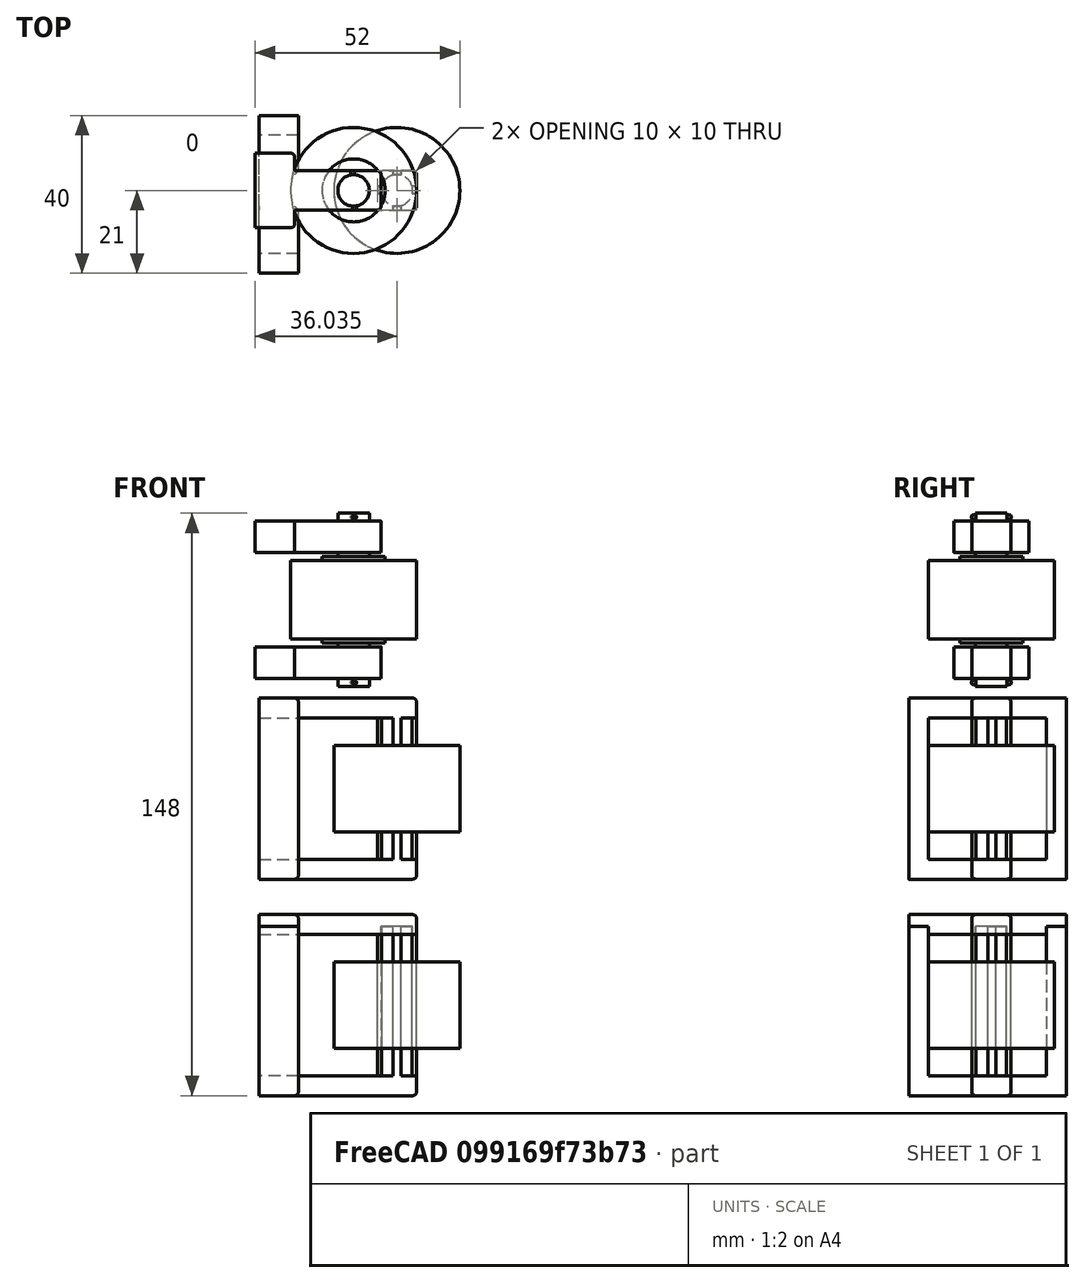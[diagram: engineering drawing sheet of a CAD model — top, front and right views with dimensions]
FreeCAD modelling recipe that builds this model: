
FCSTD DOCUMENT  (FreeCAD 0.17R13541 (Git))
Label: Electrical Tape Holder
License: All rights reserved
LicenseURL: http://en.wikipedia.org/wiki/All_rights_reserved
objects: Part::Box×98, Part::Cut×44, Part::MultiFuse×40, Part::Cylinder×35, Part::Fillet×17
note: 234 computed .brp shape members not serialized (recipe doc carries the construction recipe); baked Part::Feature solids carry a one-line shape summary decoded from their .brp

FEATURE [Part::Cylinder] Cylinder  label="Tape Holder"
  Angle = 360
  AttacherType = Attacher::AttachEngine3D
  Height = 22
  Placement = pos=(0,0,-1) rot=(0,0,1;0rad)
  Radius = 16
FEATURE [Part::Cylinder] Cylinder002  label="Tape Rotation Bar"
  Angle = 360
  AttacherType = Attacher::AttachEngine3D
  Height = 22
  Placement = pos=(0,0,-1) rot=(0,0,1;0rad)
  Radius = 8
FEATURE [Part::Cylinder] Cylinder003  label="Tape Rotation Bar Support"
  Angle = 360
  AttacherType = Attacher::AttachEngine3D
  Height = 44
  Placement = pos=(0,0,-12) rot=(0,0,1;0rad)
  Radius = 4
FEATURE [Part::Cylinder] Cylinder004  label="Tape Rotation Bar Support Cut Middle"
  Angle = 360
  AttacherType = Attacher::AttachEngine3D
  Height = 40
  Placement = pos=(0,0,-10) rot=(0,0,1;0rad)
  Radius = 4
FEATURE [Part::Cylinder] Cylinder005  label="Tape Rotation Bar Support Right"
  Angle = 360
  AttacherType = Attacher::AttachEngine3D
  Height = 40
  Placement = pos=(0,0,-74) rot=(0,0,1;0rad)
  Radius = 4
FEATURE [Part::Cut] Cut003  label="Middle Support"
  Base = -> Cylinder002
  Tool = -> Cylinder004
FEATURE [Part::Cylinder] Cylinder007  label="Lock In Support"
  Angle = 360
  AttacherType = Attacher::AttachEngine3D
  Height = 10
  Placement = pos=(0.26168,-4.99315,31) rot=(0.587166,-0.5572,-0.587166;4.1583rad)
  Radius = 0.5
FEATURE [Part::Cut] Cut004
  Base = -> Cylinder003
  Tool = -> Cylinder007
FEATURE [Part::Cylinder] Cylinder009  label="Lock In Support002"
  Angle = 360
  AttacherType = Attacher::AttachEngine3D
  Height = 10
  Placement = pos=(0.26168,-4.99315,-11) rot=(0.587166,-0.5572,-0.587166;4.1583rad)
  Radius = 0.5
FEATURE [Part::Cut] Cut005
  Base = -> Cut004
  Tool = -> Cylinder009
FEATURE [Part::Cylinder] Cylinder011  label="Tape Rotation Bar Support Left001"
  Angle = 360
  AttacherType = Attacher::AttachEngine3D
  Height = 40
  Placement = pos=(0,0,-10) rot=(0,0,1;0rad)
  Radius = 4
FEATURE [Part::Cylinder] Cylinder012  label="Tape Rotation Bar Support Right001"
  Angle = 360
  AttacherType = Attacher::AttachEngine3D
  Height = 40
  Placement = pos=(0,0,-10) rot=(0,0,1;0rad)
  Radius = 4
FEATURE [Part::Cylinder] Cylinder013  label="Tape Rotation Bar Support001"
  Angle = 360
  AttacherType = Attacher::AttachEngine3D
  Height = 44
  Placement = pos=(0,0,-12) rot=(0,0,1;0rad)
  Radius = 4
FEATURE [Part::Box] Box007  label="Cube Hinge002"
  AttacherType = Attacher::AttachEngine3D
  Height = 8
  Length = 17
  Placement = pos=(-10,-5,22) rot=(0,0,1;0rad)
  Width = 10
FEATURE [Part::Box] Box008  label="Land Leg 005"
  AttacherType = Attacher::AttachEngine3D
  Height = 8
  Length = 17
  Placement = pos=(-22,-5,22) rot=(0,0,1;0rad)
  Width = 10
FEATURE [Part::Box] Box009  label="Land Leg 006"
  AttacherType = Attacher::AttachEngine3D
  Height = 8
  Length = 19
  Placement = pos=(-15,-9.5,22) rot=(0,0,1;1.5708rad)
  Width = 10
FEATURE [Part::Box] Box010  label="Land Leg 007"
  AttacherType = Attacher::AttachEngine3D
  Height = 8
  Length = 17
  Placement = pos=(-22,-5,22) rot=(0,0,1;0rad)
  Width = 10
FEATURE [Part::Cylinder] Cylinder014  label="Tape Rotation Bar Support Cut Middle001"
  Angle = 360
  AttacherType = Attacher::AttachEngine3D
  Height = 40
  Placement = pos=(0,0,-10) rot=(0,0,1;0rad)
  Radius = 4
FEATURE [Part::Cylinder] Cylinder015  label="Tape Holder001"
  Angle = 360
  AttacherType = Attacher::AttachEngine3D
  Height = 20
  Radius = 16
FEATURE [Part::Cylinder] Cylinder016  label="Tape Rotation Bar001"
  Angle = 360
  AttacherType = Attacher::AttachEngine3D
  Height = 22
  Placement = pos=(0,0,-1) rot=(0,0,1;0rad)
  Radius = 8
FEATURE [Part::Cut] Cut011  label="Middle Support001"
  Base = -> Cylinder016
  Tool = -> Cylinder014
FEATURE [Part::Cylinder] Cylinder017  label="Tape Rotation Hole001"
  Angle = 360
  AttacherType = Attacher::AttachEngine3D
  Height = 22
  Placement = pos=(0,0,-1) rot=(0,0,1;0rad)
  Radius = 8
FEATURE [Part::Cut] Cut009
  Base = -> Cylinder015
  Tool = -> Cylinder017
FEATURE [Part::Box] Box011  label="Land Leg 008"
  AttacherType = Attacher::AttachEngine3D
  Height = 8
  Length = 19
  Placement = pos=(-15,-9.5,22) rot=(0,0,1;1.5708rad)
  Width = 10
FEATURE [Part::MultiFuse] Fusion002
  Shapes = -> [Box007,Box010,Box011]
FEATURE [Part::Cut] Cut010  label="Left Support001"
  Base = -> Fusion002
  Tool = -> Cylinder011
FEATURE [Part::Fillet] Fillet008
  Base = -> Cut010
  Edges = 2 edges r=1: [Edge1,Edge3]
FEATURE [Part::Fillet] Fillet005
  Base = -> Fillet008
  Edges = 2 edges r=1: [Edge45,Edge49]
FEATURE [Part::Box] Box012  label="Cube Hinge003"
  AttacherType = Attacher::AttachEngine3D
  Height = 8
  Length = 17
  Placement = pos=(-10,-5,22) rot=(0,0,1;0rad)
  Width = 10
FEATURE [Part::Cylinder] Cylinder018  label="Lock In Support004"
  Angle = 360
  AttacherType = Attacher::AttachEngine3D
  Height = 10
  Placement = pos=(0.26168,-4.99315,-11) rot=(0.587166,-0.5572,-0.587166;4.1583rad)
  Radius = 0.5
FEATURE [Part::Cylinder] Cylinder019  label="Lock In Support005"
  Angle = 360
  AttacherType = Attacher::AttachEngine3D
  Height = 10
  Placement = pos=(0.26168,-4.99315,31) rot=(0.587166,-0.5572,-0.587166;4.1583rad)
  Radius = 0.5
FEATURE [Part::Cut] Cut006
  Base = -> Cylinder013
  Tool = -> Cylinder019
FEATURE [Part::Cut] Cut007
  Base = -> Cut006
  Tool = -> Cylinder018
FEATURE [Part::Cylinder] Cylinder020  label="Lock In Support006"
  Angle = 360
  AttacherType = Attacher::AttachEngine3D
  Height = 10
  Placement = pos=(0.26168,-4.99315,31) rot=(0.587166,-0.5572,-0.587166;4.1583rad)
  Radius = 0.5
FEATURE [Part::Cylinder] Cylinder021  label="Lock In Support007"
  Angle = 360
  AttacherType = Attacher::AttachEngine3D
  Height = 10
  Placement = pos=(0.26168,-4.99315,-11) rot=(0.587166,-0.5572,-0.587166;4.1583rad)
  Radius = 0.5
FEATURE [Part::MultiFuse] Fusion003
  Placement = pos=(0,0,-32) rot=(0,0,1;0rad)
  Shapes = -> [Box012,Box008,Box009]
FEATURE [Part::Cut] Cut008  label="Right Support001"
  Base = -> Fusion003
  Tool = -> Cylinder012
FEATURE [Part::Fillet] Fillet006
  Base = -> Cut008
  Edges = 2 edges r=1: [Edge1,Edge3]
FEATURE [Part::Fillet] Fillet009
  Base = -> Fillet006
  Edges = 1 edges r=1: [Edge49]
FEATURE [Part::Fillet] Fillet007
  Base = -> Fillet009
  Edges = 1 edges r=1: [Edge28]
FEATURE [Part::Cut] Cut012  label="Rotation Lock"
  Base = -> Cut003
  Placement = pos=(0,0,-64) rot=(0,0,1;0rad)
  Tool = -> Cut005
FEATURE [Part::Box] Box  label="Middle Lock In Bar Cross 1"
  AttacherType = Attacher::AttachEngine3D
  Height = 40
  Length = 10
  Placement = pos=(-1,5,-74) rot=(0,0,-1;1.5708rad)
  Width = 2
FEATURE [Part::Box] Box013  label="Middle Lock In Bar Cross 2"
  AttacherType = Attacher::AttachEngine3D
  Height = 40
  Length = 10
  Placement = pos=(5.03528,1.1363,-74) rot=(0,0,-1;3.14159rad)
  Width = 2
FEATURE [Part::Cylinder] Cylinder022  label="Tape Rotation Bar Support Right002"
  Angle = 360
  AttacherType = Attacher::AttachEngine3D
  Height = 40
  Placement = pos=(0,0,-74) rot=(0,0,1;0rad)
  Radius = 4
FEATURE [Part::Box] Box014  label="Middle Lock In Bar Cross 003"
  AttacherType = Attacher::AttachEngine3D
  Height = 19
  Length = 10
  Placement = pos=(5.03528,1.1363,-65) rot=(0,0,1;3.14159rad)
  Width = 2
FEATURE [Part::Box] Box015  label="Middle Lock In Bar Cross 004"
  AttacherType = Attacher::AttachEngine3D
  Height = 19
  Length = 10
  Placement = pos=(-1,5,-65) rot=(0,0,-1;1.5708rad)
  Width = 2
FEATURE [Part::MultiFuse] Fusion005  label="Rotation Lock Bar Cutout"
  Shapes = -> [Cylinder022,Box015,Box014]
FEATURE [Part::Cut] Cut013  label="Rotation Lock001"
  Base = -> Cut012
  Tool = -> Fusion005
FEATURE [Part::Cylinder] Cylinder023  label="Tape Rotation Bar Support Right003"
  Angle = 360
  AttacherType = Attacher::AttachEngine3D
  Height = 40
  Placement = pos=(0,0,-74) rot=(0,0,1;0rad)
  Radius = 4
FEATURE [Part::Box] Box016  label="Middle Lock In Bar Cross 005"
  AttacherType = Attacher::AttachEngine3D
  Height = 40
  Length = 10
  Placement = pos=(5.03528,1.1363,-74) rot=(0,0,1;3.14159rad)
  Width = 2
FEATURE [Part::Box] Box017  label="Middle Lock In Bar Cross 006"
  AttacherType = Attacher::AttachEngine3D
  Height = 40
  Length = 10
  Placement = pos=(-1,5,-74) rot=(0,0,-1;1.5708rad)
  Width = 2
FEATURE [Part::MultiFuse] Fusion006  label="Rotion Lock Bar001"
  Shapes = -> [Cylinder023,Box017,Box016]
FEATURE [Part::Cut] Cut014  label="Rotation Gear"
  Base = -> Cut013
  Placement = pos=(0,0,64) rot=(0,0,1;0rad)
  Tool = -> Fusion006
FEATURE [Part::MultiFuse] Fusion007  label="Rotation Gear001"
  Placement = pos=(0,0,-3) rot=(0,0,1;0rad)
  Shapes = -> [Cylinder,Cut014]
FEATURE [Part::Cylinder] Cylinder024  label="Tape Rotation Bar Support Right004"
  Angle = 360
  AttacherType = Attacher::AttachEngine3D
  Height = 40
  Placement = pos=(0,0,-74) rot=(0,0,1;0rad)
  Radius = 4
FEATURE [Part::Box] Box018  label="Middle Lock In Bar Cross 007"
  AttacherType = Attacher::AttachEngine3D
  Height = 40
  Length = 10
  Placement = pos=(5.03528,1.1363,-74) rot=(0,0,1;3.14159rad)
  Width = 2
FEATURE [Part::Box] Box019  label="Middle Lock In Bar Cross 008"
  AttacherType = Attacher::AttachEngine3D
  Height = 40
  Length = 10
  Placement = pos=(-1,5,-74) rot=(0,0,-1;1.5708rad)
  Width = 2
FEATURE [Part::MultiFuse] Fusion008  label="Rotation Jock Cut"
  Placement = pos=(0,0,61) rot=(0,0,1;0rad)
  Shapes = -> [Cylinder024,Box019,Box018]
FEATURE [Part::Cut] Cut  label="Middle Drive Wheel"
  Base = -> Fusion007
  Placement = pos=(11,0,-6) rot=(0,0,1;0rad)
  Tool = -> Fusion008
FEATURE [Part::Box] Box020  label="Cube"
  AttacherType = Attacher::AttachEngine3D
  Height = 40
  Length = 5
  Placement = pos=(-35,-5,-17) rot=(0,1,0;1.5708rad)
  Width = 10
FEATURE [Part::MultiFuse] Fusion  label="Rotation Jock"
  Placement = pos=(0,0,55) rot=(0,0,1;0rad)
  Shapes = -> [Cylinder005,Box,Box013]
FEATURE [Part::Box] Box022  label="Cube002"
  AttacherType = Attacher::AttachEngine3D
  Height = 5
  Length = 5
  Placement = pos=(-3,4,19) rot=(0,0,1;0rad)
  Width = 5
FEATURE [Part::Box] Box023  label="Cube003"
  AttacherType = Attacher::AttachEngine3D
  Height = 5
  Length = 5
  Placement = pos=(-3,-9,19) rot=(0,0,1;0rad)
  Width = 5
FEATURE [Part::Box] Box024  label="Cube004"
  AttacherType = Attacher::AttachEngine3D
  Height = 5
  Length = 5
  Placement = pos=(4,-2,19) rot=(0,0,1;0rad)
  Width = 5
FEATURE [Part::Box] Box025  label="Cube005"
  AttacherType = Attacher::AttachEngine3D
  Height = 5
  Length = 5
  Placement = pos=(-9,-2,19) rot=(0,0,1;0rad)
  Width = 5
FEATURE [Part::MultiFuse] Fusion009
  Shapes = -> [Box023,Box024,Box025,Box022]
FEATURE [Part::Box] Box026  label="Cube006"
  AttacherType = Attacher::AttachEngine3D
  Height = 5
  Length = 5
  Placement = pos=(-9,-2,19) rot=(0,0,1;0rad)
  Width = 5
FEATURE [Part::Box] Box027  label="Cube007"
  AttacherType = Attacher::AttachEngine3D
  Height = 5
  Length = 5
  Placement = pos=(-3,4,19) rot=(0,0,1;0rad)
  Width = 5
FEATURE [Part::Box] Box028  label="Cube008"
  AttacherType = Attacher::AttachEngine3D
  Height = 5
  Length = 5
  Placement = pos=(-3,-9,19) rot=(0,0,1;0rad)
  Width = 5
FEATURE [Part::Box] Box029  label="Cube009"
  AttacherType = Attacher::AttachEngine3D
  Height = 5
  Length = 5
  Placement = pos=(4,-2,19) rot=(0,0,1;0rad)
  Width = 5
FEATURE [Part::MultiFuse] Fusion010
  Placement = pos=(0,0,-41) rot=(0,0,1;0rad)
  Shapes = -> [Box028,Box029,Box026,Box027]
FEATURE [Part::Cut] Cut015
  Base = -> Fusion
  Tool = -> Fusion009
FEATURE [Part::Cut] Cut016
  Base = -> Cut015
  Tool = -> Fusion010
FEATURE [Part::Box] Box030  label="Cube010"
  AttacherType = Attacher::AttachEngine3D
  Height = 40
  Length = 5
  Placement = pos=(-35,-5,24) rot=(0,1,0;1.5708rad)
  Width = 10
FEATURE [Part::Box] Box031  label="Cube011"
  AttacherType = Attacher::AttachEngine3D
  Height = 40
  Length = 10
  Placement = pos=(-25,-21,19) rot=(0,-0.707107,-0.707107;3.14159rad)
  Width = 5
FEATURE [Part::Box] Box032  label="Cube012"
  AttacherType = Attacher::AttachEngine3D
  Height = 40
  Length = 10
  Placement = pos=(-25,-21,-22) rot=(0,0.707107,0.707107;3.14159rad)
  Width = 5
FEATURE [Part::Cylinder] Cylinder025  label="Tape Rotation Bar Support Right005"
  Angle = 360
  AttacherType = Attacher::AttachEngine3D
  Height = 40
  Placement = pos=(0,0,-74) rot=(0,0,1;0rad)
  Radius = 4
FEATURE [Part::Box] Box033  label="Cube013"
  AttacherType = Attacher::AttachEngine3D
  Height = 5
  Length = 5
  Placement = pos=(-3,4,19) rot=(0,0,1;0rad)
  Width = 5
FEATURE [Part::Box] Box034  label="Cube014"
  AttacherType = Attacher::AttachEngine3D
  Height = 5
  Length = 5
  Placement = pos=(-9,-2,19) rot=(0,0,1;0rad)
  Width = 5
FEATURE [Part::Box] Box035  label="Cube015"
  AttacherType = Attacher::AttachEngine3D
  Height = 5
  Length = 5
  Placement = pos=(-3,-9,19) rot=(0,0,1;0rad)
  Width = 5
FEATURE [Part::Box] Box036  label="Cube016"
  AttacherType = Attacher::AttachEngine3D
  Height = 5
  Length = 5
  Placement = pos=(4,-2,19) rot=(0,0,1;0rad)
  Width = 5
FEATURE [Part::Box] Box037  label="Cube017"
  AttacherType = Attacher::AttachEngine3D
  Height = 5
  Length = 5
  Placement = pos=(-9,-2,19) rot=(0,0,1;0rad)
  Width = 5
FEATURE [Part::MultiFuse] Fusion013
  Placement = pos=(0,0,-41) rot=(0,0,1;0rad)
  Shapes = -> [Box035,Box036,Box034,Box033]
FEATURE [Part::Box] Box038  label="Middle Lock In Bar Cross 009"
  AttacherType = Attacher::AttachEngine3D
  Height = 40
  Length = 10
  Placement = pos=(5.03528,1.1363,-74) rot=(0,0,1;3.14159rad)
  Width = 2
FEATURE [Part::Box] Box039  label="Middle Lock In Bar Cross 010"
  AttacherType = Attacher::AttachEngine3D
  Height = 40
  Length = 10
  Placement = pos=(-1,5,-74) rot=(0,0,-1;1.5708rad)
  Width = 2
FEATURE [Part::MultiFuse] Fusion012  label="Rotation Jock001"
  Placement = pos=(0,0,55) rot=(0,0,1;0rad)
  Shapes = -> [Cylinder025,Box039,Box038]
FEATURE [Part::Box] Box040  label="Cube018"
  AttacherType = Attacher::AttachEngine3D
  Height = 5
  Length = 5
  Placement = pos=(-3,4,19) rot=(0,0,1;0rad)
  Width = 5
FEATURE [Part::Box] Box041  label="Cube019"
  AttacherType = Attacher::AttachEngine3D
  Height = 5
  Length = 5
  Placement = pos=(-3,-9,19) rot=(0,0,1;0rad)
  Width = 5
FEATURE [Part::Box] Box042  label="Cube020"
  AttacherType = Attacher::AttachEngine3D
  Height = 5
  Length = 5
  Placement = pos=(4,-2,19) rot=(0,0,1;0rad)
  Width = 5
FEATURE [Part::MultiFuse] Fusion011
  Shapes = -> [Box041,Box042,Box037,Box040]
FEATURE [Part::Cut] Cut017
  Base = -> Fusion012
  Tool = -> Fusion011
FEATURE [Part::Cut] Cut018
  Base = -> Cut017
  Tool = -> Fusion013
FEATURE [Part::Box] Box043  label="Cube021"
  AttacherType = Attacher::AttachEngine3D
  Height = 40
  Length = 10
  Placement = pos=(-25,-21,21) rot=(0,-1,0;3.14159rad)
  Width = 5
FEATURE [Part::Box] Box044  label="Back Support Connector"
  AttacherType = Attacher::AttachEngine3D
  Height = 40
  Length = 10
  Placement = pos=(-25,14,21) rot=(0,1,0;3.14159rad)
  Width = 5
FEATURE [Part::Cut] Cut019
  Base = -> Box020
  Tool = -> Cut018
FEATURE [Part::Cylinder] Cylinder026  label="Tape Rotation Bar Support Right006"
  Angle = 360
  AttacherType = Attacher::AttachEngine3D
  Height = 40
  Placement = pos=(0,0,-74) rot=(0,0,1;0rad)
  Radius = 4
FEATURE [Part::Box] Box045  label="Cube023"
  AttacherType = Attacher::AttachEngine3D
  Height = 5
  Length = 5
  Placement = pos=(-3,4,19) rot=(0,0,1;0rad)
  Width = 5
FEATURE [Part::Box] Box046  label="Cube024"
  AttacherType = Attacher::AttachEngine3D
  Height = 5
  Length = 5
  Placement = pos=(-9,-2,19) rot=(0,0,1;0rad)
  Width = 5
FEATURE [Part::Box] Box047  label="Cube025"
  AttacherType = Attacher::AttachEngine3D
  Height = 5
  Length = 5
  Placement = pos=(-3,-9,19) rot=(0,0,1;0rad)
  Width = 5
FEATURE [Part::Box] Box048  label="Cube026"
  AttacherType = Attacher::AttachEngine3D
  Height = 5
  Length = 5
  Placement = pos=(4,-2,19) rot=(0,0,1;0rad)
  Width = 5
FEATURE [Part::Box] Box049  label="Cube027"
  AttacherType = Attacher::AttachEngine3D
  Height = 5
  Length = 5
  Placement = pos=(-9,-2,19) rot=(0,0,1;0rad)
  Width = 5
FEATURE [Part::MultiFuse] Fusion016
  Placement = pos=(0,0,-41) rot=(0,0,1;0rad)
  Shapes = -> [Box047,Box048,Box046,Box045]
FEATURE [Part::Box] Box050  label="Middle Lock In Bar Cross 011"
  AttacherType = Attacher::AttachEngine3D
  Height = 40
  Length = 10
  Placement = pos=(5.03528,1.1363,-74) rot=(0,0,1;3.14159rad)
  Width = 2
FEATURE [Part::Box] Box051  label="Middle Lock In Bar Cross 012"
  AttacherType = Attacher::AttachEngine3D
  Height = 40
  Length = 10
  Placement = pos=(-1,5,-74) rot=(0,0,-1;1.5708rad)
  Width = 2
FEATURE [Part::MultiFuse] Fusion015  label="Rotation Jock002"
  Placement = pos=(0,0,55) rot=(0,0,1;0rad)
  Shapes = -> [Cylinder026,Box051,Box050]
FEATURE [Part::Box] Box052  label="Cube028"
  AttacherType = Attacher::AttachEngine3D
  Height = 5
  Length = 5
  Placement = pos=(-3,4,19) rot=(0,0,1;0rad)
  Width = 5
FEATURE [Part::Box] Box053  label="Cube029"
  AttacherType = Attacher::AttachEngine3D
  Height = 5
  Length = 5
  Placement = pos=(-3,-9,19) rot=(0,0,1;0rad)
  Width = 5
FEATURE [Part::Box] Box054  label="Cube030"
  AttacherType = Attacher::AttachEngine3D
  Height = 5
  Length = 5
  Placement = pos=(4,-2,19) rot=(0,0,1;0rad)
  Width = 5
FEATURE [Part::MultiFuse] Fusion014
  Shapes = -> [Box053,Box054,Box049,Box052]
FEATURE [Part::Cut] Cut020
  Base = -> Fusion015
  Tool = -> Fusion014
FEATURE [Part::Cut] Cut021
  Base = -> Cut020
  Tool = -> Fusion016
FEATURE [Part::Cut] Cut022
  Base = -> Box030
  Tool = -> Cut021
FEATURE [Part::Box] Box055  label="Cube031"
  AttacherType = Attacher::AttachEngine3D
  Height = 40
  Length = 10
  Placement = pos=(-25,-21,21) rot=(0,1,0;3.14159rad)
  Width = 5
FEATURE [Part::Cut] Cut023
  Base = -> Box032
  Tool = -> Box043
FEATURE [Part::Box] Box056  label="Cube032"
  AttacherType = Attacher::AttachEngine3D
  Height = 40
  Length = 10
  Placement = pos=(-25,-21,21) rot=(0,1,0;3.14159rad)
  Width = 5
FEATURE [Part::Cut] Cut024
  Base = -> Box031
  Tool = -> Box056
FEATURE [Part::Box] Box057  label="Cube033"
  AttacherType = Attacher::AttachEngine3D
  Height = 40
  Length = 10
  Placement = pos=(-25,14,21) rot=(0,1,0;3.14159rad)
  Width = 5
FEATURE [Part::Cut] Cut025
  Base = -> Cut023
  Tool = -> Box057
FEATURE [Part::Box] Box058  label="Cube034"
  AttacherType = Attacher::AttachEngine3D
  Height = 40
  Length = 10
  Placement = pos=(-25,14,21) rot=(0,1,0;3.14159rad)
  Width = 5
FEATURE [Part::Cut] Cut026
  Base = -> Cut024
  Tool = -> Box058
FEATURE [Part::Fillet] Fillet
  Base = -> Cut022
  Edges = 2 edges r=1: [Edge8,Edge10]
FEATURE [Part::Fillet] Fillet010
  Base = -> Cut019
  Edges = 2 edges r=1: [Edge17,Edge42]
FEATURE [Part::Fillet] Fillet011
  Base = -> Fillet010
  Edges = 1 edges r=1: [Edge9]
FEATURE [Part::Fillet] Fillet012
  Base = -> Fillet
  Edges = 1 edges r=1: [Edge4]
FEATURE [Part::Fillet] Fillet013
  Base = -> Cut025
  Edges = 1 edges r=1: [Edge8]
FEATURE [Part::Fillet] Fillet014
  Base = -> Cut026
  Edges = 1 edges r=1: [Edge5]
FEATURE [Part::MultiFuse] Fusion017
  Shapes = -> [Fillet013,Fillet011]
FEATURE [Part::MultiFuse] Fusion018  label="Left Support"
  Placement = pos=(11,0,0) rot=(0,0,1;0rad)
  Shapes = -> [Fillet012,Fillet014]
FEATURE [Part::MultiFuse] Fusion019  label="Right Support"
  Shapes = -> [Cut016,Fusion017]
FEATURE [Part::MultiFuse] Fusion020
  Shapes = -> [Fusion019,Box055]
FEATURE [Part::MultiFuse] Fusion021  label="Right Support002"
  Placement = pos=(11,0,0) rot=(0,0,1;0rad)
  Shapes = -> [Fusion020,Box044]
FEATURE [Part::MultiFuse] Fusion004  label="Example Model"
  Placement = pos=(0,0,94) rot=(0,0,1;0rad)
  Shapes = -> [Cut007,Cut009,Cut011,Fillet005,Fillet007,Cylinder020,Cylinder021]
FEATURE [Part::Cylinder] Cylinder027  label="Tape Rotation Bar002"
  Angle = 360
  AttacherType = Attacher::AttachEngine3D
  Height = 22
  Placement = pos=(0,0,-1) rot=(0,0,1;0rad)
  Radius = 8
FEATURE [Part::Box] Box059  label="Cube035"
  AttacherType = Attacher::AttachEngine3D
  Height = 40
  Length = 10
  Placement = pos=(-25,-21,19) rot=(0,0.707107,0.707107;3.14159rad)
  Width = 5
FEATURE [Part::Cylinder] Cylinder028  label="Tape Holder002"
  Angle = 360
  AttacherType = Attacher::AttachEngine3D
  Height = 22
  Placement = pos=(0,0,-1) rot=(0,0,1;0rad)
  Radius = 16
FEATURE [Part::Cylinder] Cylinder029  label="Tape Rotation Bar Support002"
  Angle = 360
  AttacherType = Attacher::AttachEngine3D
  Height = 44
  Placement = pos=(0,0,-12) rot=(0,0,1;0rad)
  Radius = 4
FEATURE [Part::Box] Box060  label="Cube036"
  AttacherType = Attacher::AttachEngine3D
  Height = 40
  Length = 10
  Placement = pos=(-25,14,21) rot=(0,1,0;3.14159rad)
  Width = 5
FEATURE [Part::Cylinder] Cylinder030  label="Tape Rotation Bar Support Cut Middle002"
  Angle = 360
  AttacherType = Attacher::AttachEngine3D
  Height = 40
  Placement = pos=(0,0,-10) rot=(0,0,1;0rad)
  Radius = 4
FEATURE [Part::Cut] Cut032  label="Middle Support002"
  Base = -> Cylinder027
  Tool = -> Cylinder030
FEATURE [Part::Cylinder] Cylinder031  label="Tape Rotation Bar Support Right007"
  Angle = 360
  AttacherType = Attacher::AttachEngine3D
  Height = 40
  Placement = pos=(0,0,-74) rot=(0,0,1;0rad)
  Radius = 4
FEATURE [Part::Cylinder] Cylinder032  label="Lock In Support008"
  Angle = 360
  AttacherType = Attacher::AttachEngine3D
  Height = 10
  Placement = pos=(0.26168,-4.99315,31) rot=(0.587166,-0.5572,-0.587166;4.1583rad)
  Radius = 0.5
FEATURE [Part::Cut] Cut033
  Base = -> Cylinder029
  Tool = -> Cylinder032
FEATURE [Part::Cylinder] Cylinder033  label="Lock In Support009"
  Angle = 360
  AttacherType = Attacher::AttachEngine3D
  Height = 10
  Placement = pos=(0.26168,-4.99315,-11) rot=(0.587166,-0.5572,-0.587166;4.1583rad)
  Radius = 0.5
FEATURE [Part::Cut] Cut034
  Base = -> Cut033
  Tool = -> Cylinder033
FEATURE [Part::Cylinder] Cylinder034  label="Tape Rotation Bar Support Right008"
  Angle = 360
  AttacherType = Attacher::AttachEngine3D
  Height = 40
  Placement = pos=(0,0,-74) rot=(0,0,1;0rad)
  Radius = 4
FEATURE [Part::Box] Box061  label="Cube037"
  AttacherType = Attacher::AttachEngine3D
  Height = 5
  Length = 5
  Placement = pos=(-3,4,19) rot=(0,0,1;0rad)
  Width = 5
FEATURE [Part::Cut] Cut036  label="Rotation Lock002"
  Base = -> Cut032
  Placement = pos=(0,0,-64) rot=(0,0,1;0rad)
  Tool = -> Cut034
FEATURE [Part::Box] Box062  label="Cube038"
  AttacherType = Attacher::AttachEngine3D
  Height = 5
  Length = 5
  Placement = pos=(-3,4,19) rot=(0,0,1;0rad)
  Width = 5
FEATURE [Part::Box] Box063  label="Cube039"
  AttacherType = Attacher::AttachEngine3D
  Height = 5
  Length = 5
  Placement = pos=(-9,-2,19) rot=(0,0,1;0rad)
  Width = 5
FEATURE [Part::Box] Box064  label="Cube040"
  AttacherType = Attacher::AttachEngine3D
  Height = 5
  Length = 5
  Placement = pos=(-3,-9,19) rot=(0,0,1;0rad)
  Width = 5
FEATURE [Part::Box] Box065  label="Cube041"
  AttacherType = Attacher::AttachEngine3D
  Height = 5
  Length = 5
  Placement = pos=(4,-2,19) rot=(0,0,1;0rad)
  Width = 5
FEATURE [Part::Box] Box066  label="Cube042"
  AttacherType = Attacher::AttachEngine3D
  Height = 5
  Length = 5
  Placement = pos=(-3,-9,19) rot=(0,0,1;0rad)
  Width = 5
FEATURE [Part::Box] Box067  label="Cube043"
  AttacherType = Attacher::AttachEngine3D
  Height = 5
  Length = 5
  Placement = pos=(-9,-2,19) rot=(0,0,1;0rad)
  Width = 5
FEATURE [Part::Box] Box068  label="Cube044"
  AttacherType = Attacher::AttachEngine3D
  Height = 40
  Length = 5
  Placement = pos=(-35,-5,-17) rot=(0,1,0;1.5708rad)
  Width = 10
FEATURE [Part::MultiFuse] Fusion033
  Placement = pos=(0,0,-41) rot=(0,0,1;0rad)
  Shapes = -> [Box064,Box065,Box063,Box062]
FEATURE [Part::Box] Box069  label="Middle Lock In Bar Cross 013"
  AttacherType = Attacher::AttachEngine3D
  Height = 40
  Length = 10
  Placement = pos=(5.03528,1.1363,-74) rot=(0,0,1;3.14159rad)
  Width = 2
FEATURE [Part::Cylinder] Cylinder035  label="Tape Rotation Bar Support Right009"
  Angle = 360
  AttacherType = Attacher::AttachEngine3D
  Height = 40
  Placement = pos=(0,0,-74) rot=(0,0,1;0rad)
  Radius = 4
FEATURE [Part::Box] Box070  label="Middle Lock In Bar Cross 014"
  AttacherType = Attacher::AttachEngine3D
  Height = 19
  Length = 10
  Placement = pos=(5.03528,1.1363,-65) rot=(0,0,1;3.14159rad)
  Width = 2
FEATURE [Part::Box] Box071  label="Middle Lock In Bar Cross 015"
  AttacherType = Attacher::AttachEngine3D
  Height = 40
  Length = 10
  Placement = pos=(5.03528,1.1363,-74) rot=(0,0,1;3.14159rad)
  Width = 2
FEATURE [Part::Box] Box072  label="Middle Lock In Bar Cross 016"
  AttacherType = Attacher::AttachEngine3D
  Height = 19
  Length = 10
  Placement = pos=(-1,5,-65) rot=(0,0,-1;1.5708rad)
  Width = 2
FEATURE [Part::MultiFuse] Fusion024  label="Rotation Lock Bar Cutout001"
  Shapes = -> [Cylinder035,Box072,Box070]
FEATURE [Part::Cut] Cut044  label="Rotation Lock003"
  Base = -> Cut036
  Tool = -> Fusion024
FEATURE [Part::Cylinder] Cylinder036  label="Tape Rotation Bar Support Right010"
  Angle = 360
  AttacherType = Attacher::AttachEngine3D
  Height = 40
  Placement = pos=(0,0,-74) rot=(0,0,1;0rad)
  Radius = 4
FEATURE [Part::Box] Box073  label="Middle Lock In Bar Cross 017"
  AttacherType = Attacher::AttachEngine3D
  Height = 40
  Length = 10
  Placement = pos=(-1,5,-74) rot=(0,0,-1;1.5708rad)
  Width = 2
FEATURE [Part::MultiFuse] Fusion032  label="Rotation Jock005"
  Placement = pos=(0,0,55) rot=(0,0,1;0rad)
  Shapes = -> [Cylinder034,Box073,Box069]
FEATURE [Part::Box] Box074  label="Middle Lock In Bar Cross 018"
  AttacherType = Attacher::AttachEngine3D
  Height = 40
  Length = 10
  Placement = pos=(-1,5,-74) rot=(0,0,-1;1.5708rad)
  Width = 2
FEATURE [Part::MultiFuse] Fusion025  label="Rotion Lock Bar002"
  Shapes = -> [Cylinder036,Box074,Box071]
FEATURE [Part::Cut] Cut039  label="Rotation Gear002"
  Base = -> Cut044
  Placement = pos=(0,0,64) rot=(0,0,1;0rad)
  Tool = -> Fusion025
FEATURE [Part::MultiFuse] Fusion026  label="Rotation Gear003"
  Placement = pos=(0,0,-3) rot=(0,0,1;0rad)
  Shapes = -> [Cylinder028,Cut039]
FEATURE [Part::Cylinder] Cylinder037  label="Tape Rotation Bar Support Right011"
  Angle = 360
  AttacherType = Attacher::AttachEngine3D
  Height = 40
  Placement = pos=(0,0,-74) rot=(0,0,1;0rad)
  Radius = 4
FEATURE [Part::Box] Box075  label="Cube045"
  AttacherType = Attacher::AttachEngine3D
  Height = 5
  Length = 5
  Placement = pos=(-3,4,19) rot=(0,0,1;0rad)
  Width = 5
FEATURE [Part::Box] Box076  label="Cube046"
  AttacherType = Attacher::AttachEngine3D
  Height = 5
  Length = 5
  Placement = pos=(-3,-9,19) rot=(0,0,1;0rad)
  Width = 5
FEATURE [Part::Box] Box077  label="Cube047"
  AttacherType = Attacher::AttachEngine3D
  Height = 5
  Length = 5
  Placement = pos=(4,-2,19) rot=(0,0,1;0rad)
  Width = 5
FEATURE [Part::MultiFuse] Fusion031
  Shapes = -> [Box076,Box077,Box067,Box075]
FEATURE [Part::Cut] Cut038
  Base = -> Fusion032
  Tool = -> Fusion031
FEATURE [Part::Cut] Cut043
  Base = -> Cut038
  Tool = -> Fusion033
FEATURE [Part::Box] Box078  label="Cube048"
  AttacherType = Attacher::AttachEngine3D
  Height = 40
  Length = 5
  Placement = pos=(-35,-5,24) rot=(0,1,0;1.5708rad)
  Width = 10
FEATURE [Part::Box] Box079  label="Cube049"
  AttacherType = Attacher::AttachEngine3D
  Height = 40
  Length = 10
  Placement = pos=(-25,-21,-22) rot=(0,0.707107,0.707107;3.14159rad)
  Width = 5
FEATURE [Part::Box] Box080  label="Middle Lock In Bar Cross 019"
  AttacherType = Attacher::AttachEngine3D
  Height = 40
  Length = 10
  Placement = pos=(-1,5,-74) rot=(0,0,-1;1.5708rad)
  Width = 2
FEATURE [Part::Box] Box081  label="Middle Lock In Bar Cross 020"
  AttacherType = Attacher::AttachEngine3D
  Height = 40
  Length = 10
  Placement = pos=(5.03528,1.1363,-74) rot=(0,0,1;3.14159rad)
  Width = 2
FEATURE [Part::MultiFuse] Fusion030  label="Rotation Jock Cut001"
  Placement = pos=(0,0,61) rot=(0,0,1;0rad)
  Shapes = -> [Cylinder037,Box080,Box081]
FEATURE [Part::Cut] Cut037  label="Middle Drive Wheel001"
  Base = -> Fusion026
  Placement = pos=(0,0,-6) rot=(0,0,1;0rad)
  Tool = -> Fusion030
FEATURE [Part::Box] Box082  label="Cube050"
  AttacherType = Attacher::AttachEngine3D
  Height = 5
  Length = 5
  Placement = pos=(-9,-2,19) rot=(0,0,1;0rad)
  Width = 5
FEATURE [Part::Box] Box083  label="Cube051"
  AttacherType = Attacher::AttachEngine3D
  Height = 5
  Length = 5
  Placement = pos=(-9,-2,19) rot=(0,0,1;0rad)
  Width = 5
FEATURE [Part::Box] Box084  label="Cube052"
  AttacherType = Attacher::AttachEngine3D
  Height = 5
  Length = 5
  Placement = pos=(-3,4,19) rot=(0,0,1;0rad)
  Width = 5
FEATURE [Part::Box] Box085  label="Cube053"
  AttacherType = Attacher::AttachEngine3D
  Height = 5
  Length = 5
  Placement = pos=(-9,-2,19) rot=(0,0,1;0rad)
  Width = 5
FEATURE [Part::Box] Box086  label="Cube054"
  AttacherType = Attacher::AttachEngine3D
  Height = 5
  Length = 5
  Placement = pos=(-3,4,19) rot=(0,0,1;0rad)
  Width = 5
FEATURE [Part::Cylinder] Cylinder038  label="Tape Rotation Bar Support Right012"
  Angle = 360
  AttacherType = Attacher::AttachEngine3D
  Height = 40
  Placement = pos=(0,0,-74) rot=(0,0,1;0rad)
  Radius = 4
FEATURE [Part::Box] Box087  label="Cube055"
  AttacherType = Attacher::AttachEngine3D
  Height = 5
  Length = 5
  Placement = pos=(-3,-9,19) rot=(0,0,1;0rad)
  Width = 5
FEATURE [Part::Box] Box088  label="Cube056"
  AttacherType = Attacher::AttachEngine3D
  Height = 5
  Length = 5
  Placement = pos=(-3,-9,19) rot=(0,0,1;0rad)
  Width = 5
FEATURE [Part::Box] Box089  label="Middle Lock In Bar Cross 021"
  AttacherType = Attacher::AttachEngine3D
  Height = 40
  Length = 10
  Placement = pos=(5.03528,1.1363,-74) rot=(0,0,1;3.14159rad)
  Width = 2
FEATURE [Part::Box] Box090  label="Cube057"
  AttacherType = Attacher::AttachEngine3D
  Height = 5
  Length = 5
  Placement = pos=(4,-2,19) rot=(0,0,1;0rad)
  Width = 5
FEATURE [Part::MultiFuse] Fusion034
  Shapes = -> [Box087,Box090,Box085,Box084]
FEATURE [Part::Box] Box091  label="Back Support Connector001"
  AttacherType = Attacher::AttachEngine3D
  Height = 40
  Length = 10
  Placement = pos=(-25,14,21) rot=(0,1,0;3.14159rad)
  Width = 5
FEATURE [Part::Box] Box092  label="Cube058"
  AttacherType = Attacher::AttachEngine3D
  Height = 5
  Length = 5
  Placement = pos=(4,-2,19) rot=(0,0,1;0rad)
  Width = 5
FEATURE [Part::MultiFuse] Fusion029
  Placement = pos=(0,0,-41) rot=(0,0,1;0rad)
  Shapes = -> [Box088,Box092,Box083,Box086]
FEATURE [Part::Box] Box093  label="Middle Lock In Bar Cross 022"
  AttacherType = Attacher::AttachEngine3D
  Height = 40
  Length = 10
  Placement = pos=(5.03528,1.1363,-74) rot=(0,0,1;3.14159rad)
  Width = 2
FEATURE [Part::Box] Box094  label="Cube059"
  AttacherType = Attacher::AttachEngine3D
  Height = 40
  Length = 10
  Placement = pos=(-25,-21,21) rot=(0,1,0;3.14159rad)
  Width = 5
FEATURE [Part::Cut] Cut027
  Base = -> Box079
  Tool = -> Box094
FEATURE [Part::Box] Box095  label="Cube060"
  AttacherType = Attacher::AttachEngine3D
  Height = 5
  Length = 5
  Placement = pos=(-9,-2,19) rot=(0,0,1;0rad)
  Width = 5
FEATURE [Part::Box] Box096  label="Middle Lock In Bar Cross 023"
  AttacherType = Attacher::AttachEngine3D
  Height = 40
  Length = 10
  Placement = pos=(-1,5,-74) rot=(0,0,-1;1.5708rad)
  Width = 2
FEATURE [Part::MultiFuse] Fusion022  label="Rotation Jock003"
  Placement = pos=(0,0,55) rot=(0,0,1;0rad)
  Shapes = -> [Cylinder038,Box096,Box093]
FEATURE [Part::Box] Box097  label="Cube061"
  AttacherType = Attacher::AttachEngine3D
  Height = 40
  Length = 10
  Placement = pos=(-25,-21,21) rot=(0,1,0;3.14159rad)
  Width = 5
FEATURE [Part::Box] Box098  label="Cube062"
  AttacherType = Attacher::AttachEngine3D
  Height = 40
  Length = 10
  Placement = pos=(-25,-21,21) rot=(0,1,0;3.14159rad)
  Width = 5
FEATURE [Part::Cut] Cut028
  Base = -> Box059
  Tool = -> Box098
FEATURE [Part::Cut] Cut045
  Base = -> Cut028
  Tool = -> Box060
FEATURE [Part::Fillet] Fillet018
  Base = -> Cut045
  Edges = 1 edges r=1: [Edge5]
FEATURE [Part::Box] Box099  label="Cube063"
  AttacherType = Attacher::AttachEngine3D
  Height = 5
  Length = 5
  Placement = pos=(4,-2,19) rot=(0,0,1;0rad)
  Width = 5
FEATURE [Part::Box] Box100  label="Cube064"
  AttacherType = Attacher::AttachEngine3D
  Height = 5
  Length = 5
  Placement = pos=(-3,4,19) rot=(0,0,1;0rad)
  Width = 5
FEATURE [Part::Box] Box101  label="Cube065"
  AttacherType = Attacher::AttachEngine3D
  Height = 5
  Length = 5
  Placement = pos=(-3,-9,19) rot=(0,0,1;0rad)
  Width = 5
FEATURE [Part::MultiFuse] Fusion023
  Shapes = -> [Box101,Box099,Box095,Box100]
FEATURE [Part::Cut] Cut030
  Base = -> Fusion022
  Tool = -> Fusion023
FEATURE [Part::Cut] Cut031
  Base = -> Cut030
  Tool = -> Fusion029
FEATURE [Part::Cut] Cut035
  Base = -> Box078
  Tool = -> Cut031
FEATURE [Part::Fillet] Fillet020
  Base = -> Cut035
  Edges = 2 edges r=1: [Edge8,Edge10]
FEATURE [Part::Fillet] Fillet017
  Base = -> Fillet020
  Edges = 1 edges r=1: [Edge4]
FEATURE [Part::Box] Box102  label="Middle Lock In Bar Cross 024"
  AttacherType = Attacher::AttachEngine3D
  Height = 40
  Length = 10
  Placement = pos=(-1,5,-74) rot=(0,0,-1;1.5708rad)
  Width = 2
FEATURE [Part::MultiFuse] Fusion027  label="Rotation Jock004"
  Placement = pos=(0,0,55) rot=(0,0,1;0rad)
  Shapes = -> [Cylinder031,Box102,Box089]
FEATURE [Part::Cut] Cut040
  Base = -> Fusion027
  Tool = -> Fusion034
FEATURE [Part::Box] Box103  label="Cube066"
  AttacherType = Attacher::AttachEngine3D
  Height = 5
  Length = 5
  Placement = pos=(4,-2,19) rot=(0,0,1;0rad)
  Width = 5
FEATURE [Part::MultiFuse] Fusion028
  Placement = pos=(0,0,-41) rot=(0,0,1;0rad)
  Shapes = -> [Box066,Box103,Box082,Box061]
FEATURE [Part::Cut] Cut042
  Base = -> Cut040
  Tool = -> Fusion028
FEATURE [Part::Cut] Cut029
  Base = -> Box068
  Tool = -> Cut042
FEATURE [Part::Fillet] Fillet016
  Base = -> Cut029
  Edges = 2 edges r=1: [Edge17,Edge42]
FEATURE [Part::Fillet] Fillet015
  Base = -> Fillet016
  Edges = 1 edges r=1: [Edge9]
FEATURE [Part::Box] Box104  label="Cube067"
  AttacherType = Attacher::AttachEngine3D
  Height = 40
  Length = 10
  Placement = pos=(-25,14,21) rot=(0,1,0;3.14159rad)
  Width = 5
FEATURE [Part::Cut] Cut041
  Base = -> Cut027
  Tool = -> Box104
FEATURE [Part::Fillet] Fillet019
  Base = -> Cut041
  Edges = 1 edges r=1: [Edge8]
FEATURE [Part::MultiFuse] Fusion037  label="Left Support002"
  Shapes = -> [Fillet017,Fillet018]
FEATURE [Part::MultiFuse] Fusion038
  Shapes = -> [Fillet019,Fillet015]
FEATURE [Part::MultiFuse] Fusion039  label="Right Support004"
  Shapes = -> [Cut043,Fusion038]
FEATURE [Part::MultiFuse] Fusion040
  Shapes = -> [Fusion039,Box097]
FEATURE [Part::MultiFuse] Fusion035  label="Right Support003"
  Shapes = -> [Fusion040,Box091]
FEATURE [Part::MultiFuse] Fusion036  label="Example Model 2"
  Placement = pos=(11,0,55) rot=(0,0,1;0rad)
  Shapes = -> [Cut037,Fusion037,Fusion035]
